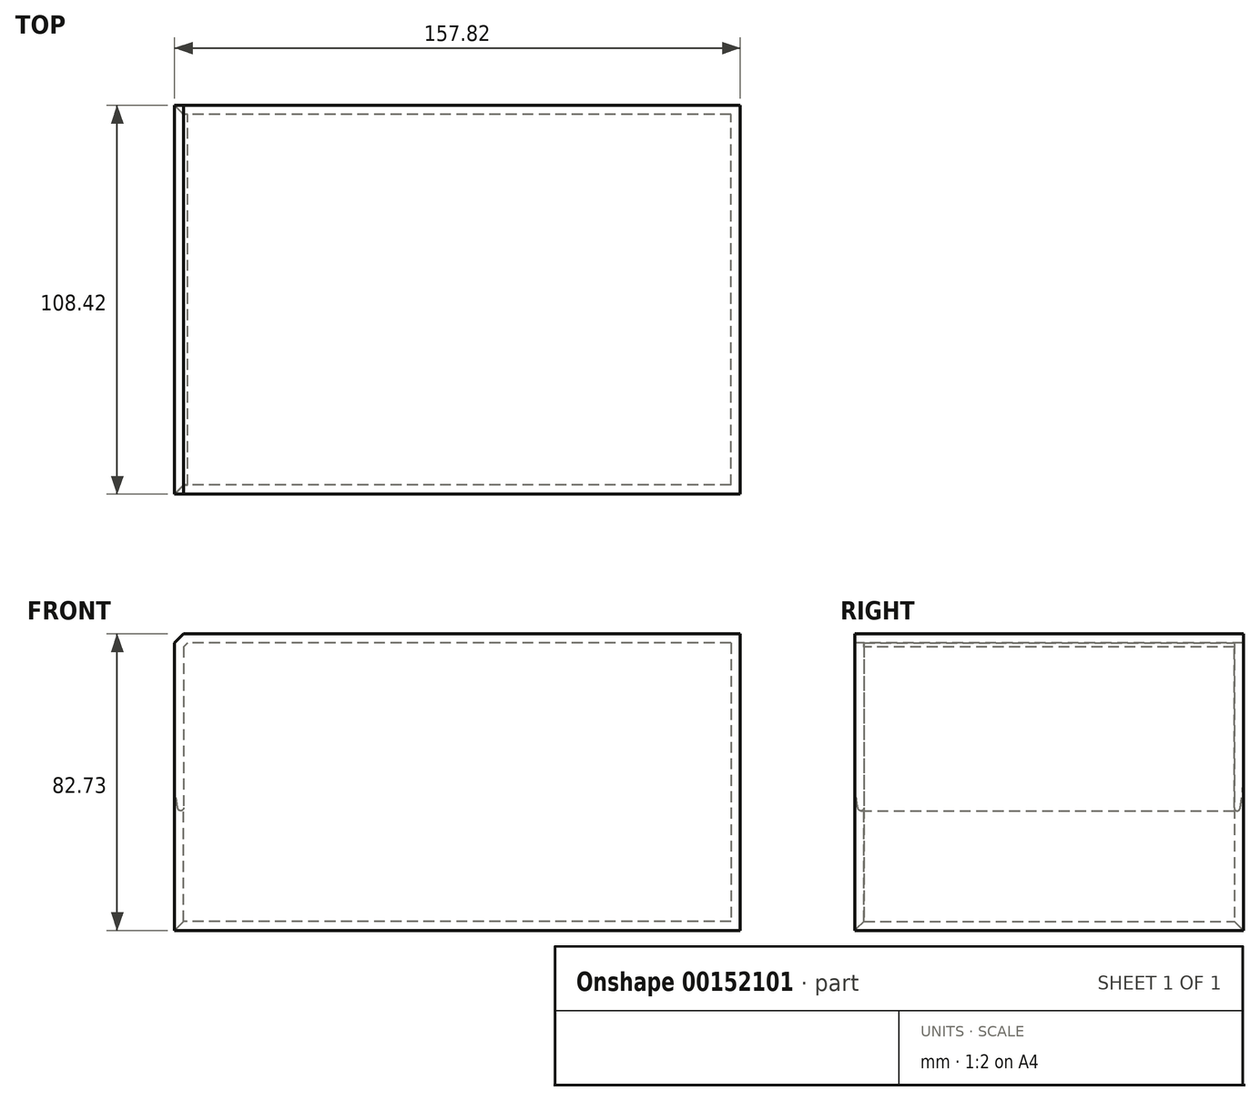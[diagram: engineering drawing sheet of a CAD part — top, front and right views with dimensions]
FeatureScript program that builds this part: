
annotation { "Feature Type Name" : "Feature", "Feature Type Description" : "" }
export const myFeature = defineFeature(function(context is Context, id is Id, definition is map)
    precondition{}
    {
        {
            var Q0;
            Q0=qCreatedBy(makeId("Top.planeOp"),FACE);
            var sketch = newSketch(context, id + "F0", { "sketchPlane" : qUnion([Q0])});
            skLineSegment(sketch, "E0.bottom", {"start": v(80.18, -54.21) * mm, "end": v(-80.18, -54.21) * mm});
            skLineSegment(sketch, "E0.top", {"start": v(80.18, 54.21) * mm, "end": v(-80.18, 54.21) * mm});
            skLineSegment(sketch, "E0.left", {"start": v(80.18, -54.21) * mm, "end": v(80.18, 54.21) * mm});
            skLineSegment(sketch, "E0.right", {"start": v(-80.18, -54.21) * mm, "end": v(-80.18, 54.21) * mm});
            skPoint(sketch, "E0.middle", {"position": v(0, 0) * mm});
            skSolve(sketch);
        }
        {
            var Q0;
            Q0=makeQuery(id+"F0.imprint","IMPRINT",FACE,{"disambiguationData":[TD([[makeQuery(id+"F0.imprint","IMPRINT",EDGE,{"derivedFrom":sQuery(id+"F0.wireOp",EDGE,"E0.bottom")}),-1.0]])]});
            extrude(context, id + "F1", {"entities" : qUnion([Q0]), "depth" : 82.73 * mm});
        }
        {
            var Q0;
            Q0=makeQuery(id+"F1.opExtrude","SWEPT_FACE",FACE,{"disambiguationData":[OSD([sQuery(id+"F0.wireOp",EDGE,"E0.right")])]});
            shell(context, id + "F2", {"entities" : qUnion([Q0]), "thickness" : 2.54 * mm});
        }
        {
            var Q0;
            Q0=makeQuery(id+"F1.opExtrude","CAP_EDGE",EDGE,{"disambiguationData":[OSD([sQuery(id+"F0.wireOp",EDGE,"E0.right")])],"isStart":false});
            var Q1;
            {var subQ0=sQuery(id+"F0.wireOp",EDGE,"E0.right");Q1=makeQuery(id+"F2.opShell","OFFSET_EDGE",EDGE,{"disambiguationData":[OSD([subQ0]),TDD([makeQuery(id+"F1.opExtrude","CAP_EDGE",EDGE,{"disambiguationData":[OSD([subQ0])],"isStart":true})])]});}
            chamfer(context, id + "F3", {"entities" : qUnion([Q0, Q1]), "width" : 5.08 * mm, "tangentPropagation" : true});
        }
        {
            var Q0;
            Q0=makeQuery(id+"F2.opShell","OFFSET_EDGE",EDGE,{"disambiguationData":[OSD([sQuery(id+"F0.wireOp",EDGE,"E0.bottom"),sQuery(id+"F0.wireOp",EDGE,"E0.right")])]});
            var Q1;
            Q1=makeQuery(id+"F2.opShell","OFFSET_EDGE",EDGE,{"disambiguationData":[OSD([sQuery(id+"F0.wireOp",EDGE,"E0.top"),sQuery(id+"F0.wireOp",EDGE,"E0.right")])]});
            chamfer(context, id + "F4", {"entities" : qUnion([Q0, Q1]), "width" : 5.08 * mm, "tangentPropagation" : true});
        }
        {
            var Q0;
            Q0=makeQuery(id+"F1.opExtrude","CAP_FACE",FACE,{"disambiguationData":[OSD([sQuery(id+"F0.wireOp",EDGE,"E0.bottom"),sQuery(id+"F0.wireOp",EDGE,"E0.top"),sQuery(id+"F0.wireOp",EDGE,"E0.left"),sQuery(id+"F0.wireOp",EDGE,"E0.right")])],"isStart":false});
            var sketch = newSketch(context, id + "F5", { "sketchPlane" : qUnion([Q0])});
            skLineSegment(sketch, "E1.bottom", {"start": v(80.18, -20.25) * mm, "end": v(45.65, -20.25) * mm});
            skLineSegment(sketch, "E1.top", {"start": v(80.18, 20.25) * mm, "end": v(45.65, 20.25) * mm});
            skLineSegment(sketch, "E1.left", {"start": v(80.18, -20.25) * mm, "end": v(80.18, 20.25) * mm});
            skLineSegment(sketch, "E1.right", {"start": v(45.65, -20.25) * mm, "end": v(45.65, 20.25) * mm});
            skPoint(sketch, "E1.middle", {"position": v(62.91, 0) * mm});
            skPoint(sketch, "E1.middle.positionSnap0", {"position": v(80.18, 0) * mm});
            skPoint(sketch, "E1.centerSnap0", {"position": v(80.18, 0) * mm});
            skSolve(sketch);
        }
        {
            var Q0;
            Q0 = qSketchRegion(id + "F5", true);
            var Q1;
            Q1=makeQuery(id+"F5.imprint","IMPRINT",FACE,{"disambiguationData":[TD([[makeQuery(id+"F5.imprint","IMPRINT",EDGE,{"derivedFrom":sQuery(id+"F5.wireOp",EDGE,"E1.bottom")}),-1.0]])]});
            var Q2;
            {var subQ0=sQuery(id+"F0.wireOp",EDGE,"E0.right");var subQ1=sQuery(id+"F0.wireOp",EDGE,"E0.left");var subQ2=sQuery(id+"F0.wireOp",EDGE,"E0.top");var subQ3=sQuery(id+"F0.wireOp",EDGE,"E0.bottom");Q2=makeQuery(id+"F2.opShell","OFFSET_FACE",FACE,{"disambiguationData":[OSD([subQ3,subQ2,subQ1,subQ0]),TDD([makeQuery(id+"F1.opExtrude","CAP_FACE",FACE,{"disambiguationData":[OSD([subQ3,subQ2,subQ1,subQ0])],"isStart":false})])]});}
            extrude(context, id + "F6", {"entities" : qUnion([Q0, Q1, Q2]), "operationType" : NewBodyOperationType.ADD, "oppositeDirection" : true, "depth" : 52.9 * mm});
        }
        {
            var Q0;
            Q0=makeQuery(id+"F6.opExtrude","CAP_FACE",FACE,{"disambiguationData":[OSD([sQuery(id+"F0.wireOp",EDGE,"E0.bottom"),sQuery(id+"F0.wireOp",EDGE,"E0.top"),sQuery(id+"F0.wireOp",EDGE,"E0.left"),sQuery(id+"F0.wireOp",EDGE,"E0.right")])],"isStart":false});
            shell(context, id + "F7", {"entities" : qUnion([Q0]), "thickness" : 2.54 * mm});
        }
        {
            var Q0;
            {var subQ0=sQuery(id+"F0.wireOp",EDGE,"E0.right");var subQ1=sQuery(id+"F0.wireOp",EDGE,"E0.left");var subQ2=sQuery(id+"F0.wireOp",EDGE,"E0.top");var subQ3=sQuery(id+"F0.wireOp",EDGE,"E0.bottom");Q0=makeQuery(id+"F6.opExtrude","CAP_EDGE",EDGE,{"disambiguationData":[OSD([subQ3,subQ2,subQ1,subQ0]),TDD([makeQuery(id+"F3.opChamfer","BLEND_EDGE",EDGE,{"blendedFrom":[makeQuery(id+"F1.opExtrude","CAP_EDGE",EDGE,{"disambiguationData":[OSD([subQ0])],"isStart":false}),makeQuery(id+"F2.opShell","OFFSET_FACE",FACE,{"disambiguationData":[OSD([subQ3,subQ2,subQ1,subQ0]),TDD([makeQuery(id+"F1.opExtrude","CAP_FACE",FACE,{"disambiguationData":[OSD([subQ3,subQ2,subQ1,subQ0])],"isStart":false})])]})],"blendedInto":[makeQuery(id+"F2.opShell","OFFSET_FACE",FACE,{"disambiguationData":[OSD([subQ3,subQ2,subQ1,subQ0]),TDD([makeQuery(id+"F1.opExtrude","CAP_FACE",FACE,{"disambiguationData":[OSD([subQ3,subQ2,subQ1,subQ0])],"isStart":false})])]})]})])],"isStart":false});}
            fillet(context, id + "F8", {"entities" : qUnion([Q0]), "radius" : 57.31 * mm, "tangentPropagation" : true, "allowEdgeOverflow" : false});
        }
        {
            var Q0;
            {var subQ0=sQuery(id+"F0.wireOp",EDGE,"E0.right");var subQ1=sQuery(id+"F0.wireOp",EDGE,"E0.left");var subQ2=sQuery(id+"F0.wireOp",EDGE,"E0.top");var subQ3=sQuery(id+"F0.wireOp",EDGE,"E0.bottom");var subQ4=makeQuery(id+"F3.opChamfer","BLEND_EDGE",EDGE,{"blendedFrom":[makeQuery(id+"F1.opExtrude","CAP_EDGE",EDGE,{"disambiguationData":[OSD([subQ0])],"isStart":false}),makeQuery(id+"F2.opShell","OFFSET_FACE",FACE,{"disambiguationData":[OSD([subQ3,subQ2,subQ1,subQ0]),TDD([makeQuery(id+"F1.opExtrude","CAP_FACE",FACE,{"disambiguationData":[OSD([subQ3,subQ2,subQ1,subQ0])],"isStart":false})])]})],"blendedInto":[makeQuery(id+"F2.opShell","OFFSET_FACE",FACE,{"disambiguationData":[OSD([subQ3,subQ2,subQ1,subQ0]),TDD([makeQuery(id+"F1.opExtrude","CAP_FACE",FACE,{"disambiguationData":[OSD([subQ3,subQ2,subQ1,subQ0])],"isStart":false})])]})]});Q0=makeQuery(id+"F8.opFillet","BLEND_EDGE",EDGE,{"blendedFrom":[makeQuery(id+"F6.opExtrude","CAP_EDGE",EDGE,{"disambiguationData":[OSD([subQ3,subQ2,subQ1,subQ0]),TDD([subQ4])],"isStart":false}),makeQuery(id+"F7.opShell","OFFSET_FACE",FACE,{"disambiguationData":[OSD([subQ3,subQ2,subQ1,subQ0]),TDD([makeQuery(id+"F6.opExtrude","SWEPT_FACE",FACE,{"disambiguationData":[OSD([subQ3,subQ2,subQ1,subQ0]),TDD([subQ4])]})])]})],"blendedInto":[makeQuery(id+"F7.opShell","OFFSET_FACE",FACE,{"disambiguationData":[OSD([subQ3,subQ2,subQ1,subQ0]),TDD([makeQuery(id+"F6.opExtrude","SWEPT_FACE",FACE,{"disambiguationData":[OSD([subQ3,subQ2,subQ1,subQ0]),TDD([subQ4])]})])]})]});}
            fillet(context, id + "F9", {"entities" : qUnion([Q0]), "radius" : 0.83 * mm, "tangentPropagation" : true, "allowEdgeOverflow" : false});
        }
    });
